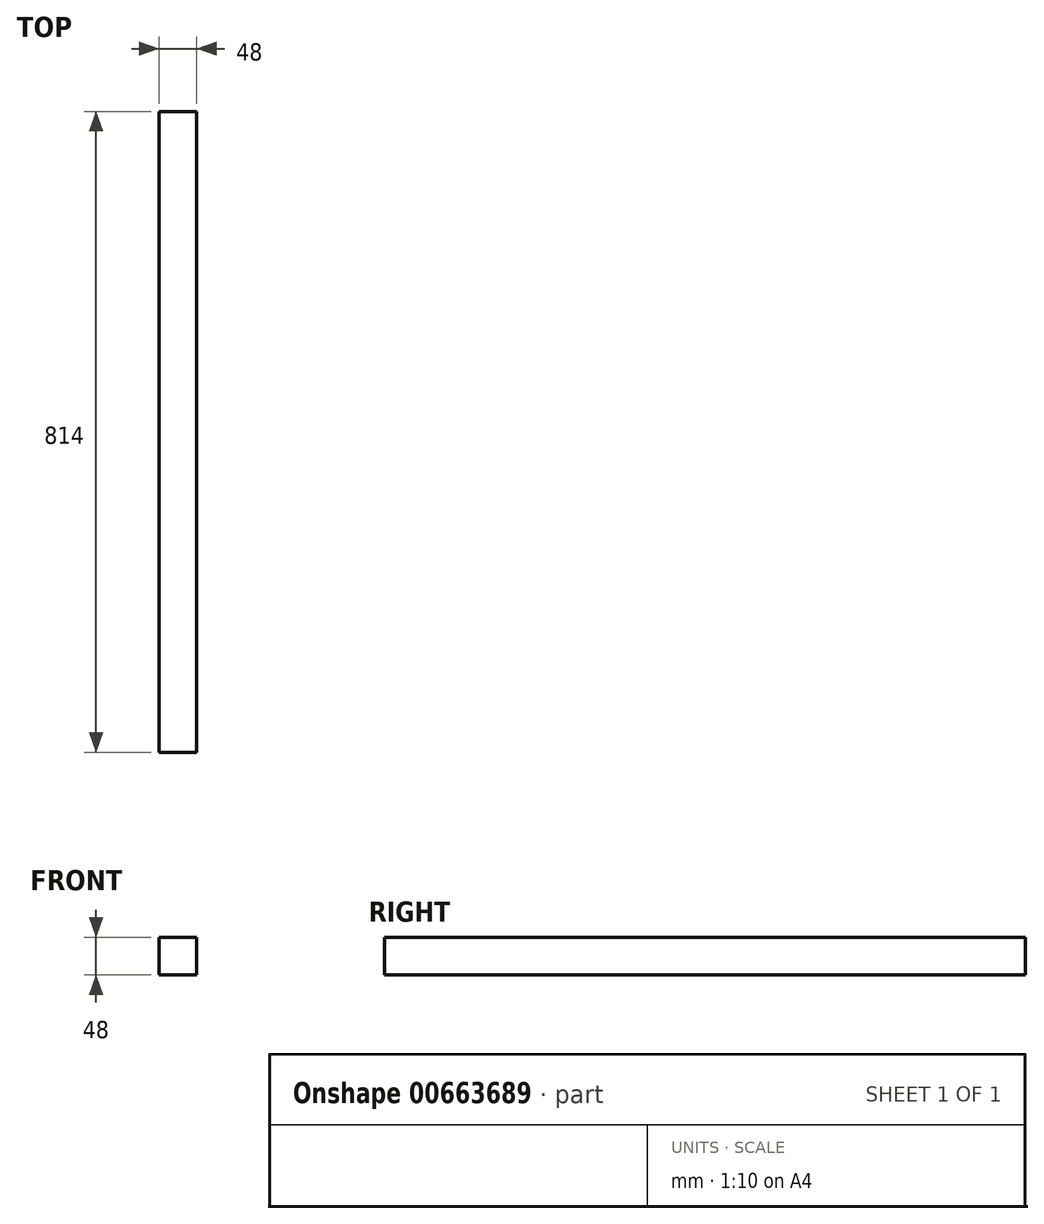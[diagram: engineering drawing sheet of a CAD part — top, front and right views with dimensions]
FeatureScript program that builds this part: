
annotation { "Feature Type Name" : "Feature", "Feature Type Description" : "" }
export const myFeature = defineFeature(function(context is Context, id is Id, definition is map)
    precondition{}
    {
        {
            var Q0;
            Q0=qCreatedBy(makeId("Front.planeOp"),FACE);
            var sketch = newSketch(context, id + "F0", { "sketchPlane" : qUnion([Q0])});
            skLineSegment(sketch, "E0.bottom", {"start": v(0, 0) * mm, "end": v(48, 0) * mm});
            skLineSegment(sketch, "E0.top", {"start": v(0, 48) * mm, "end": v(48, 48) * mm});
            skLineSegment(sketch, "E0.left", {"start": v(0, 0) * mm, "end": v(0, 48) * mm});
            skLineSegment(sketch, "E0.right", {"start": v(48, 0) * mm, "end": v(48, 48) * mm});
            skSolve(sketch);
        }
        {
            var Q0;
            Q0 = qSketchRegion(id + "F0", true);
            extrude(context, id + "F1", {"entities" : qUnion([Q0]), "depth" : 814 * mm, "offsetDistance" : 25 * mm});
        }
    });
